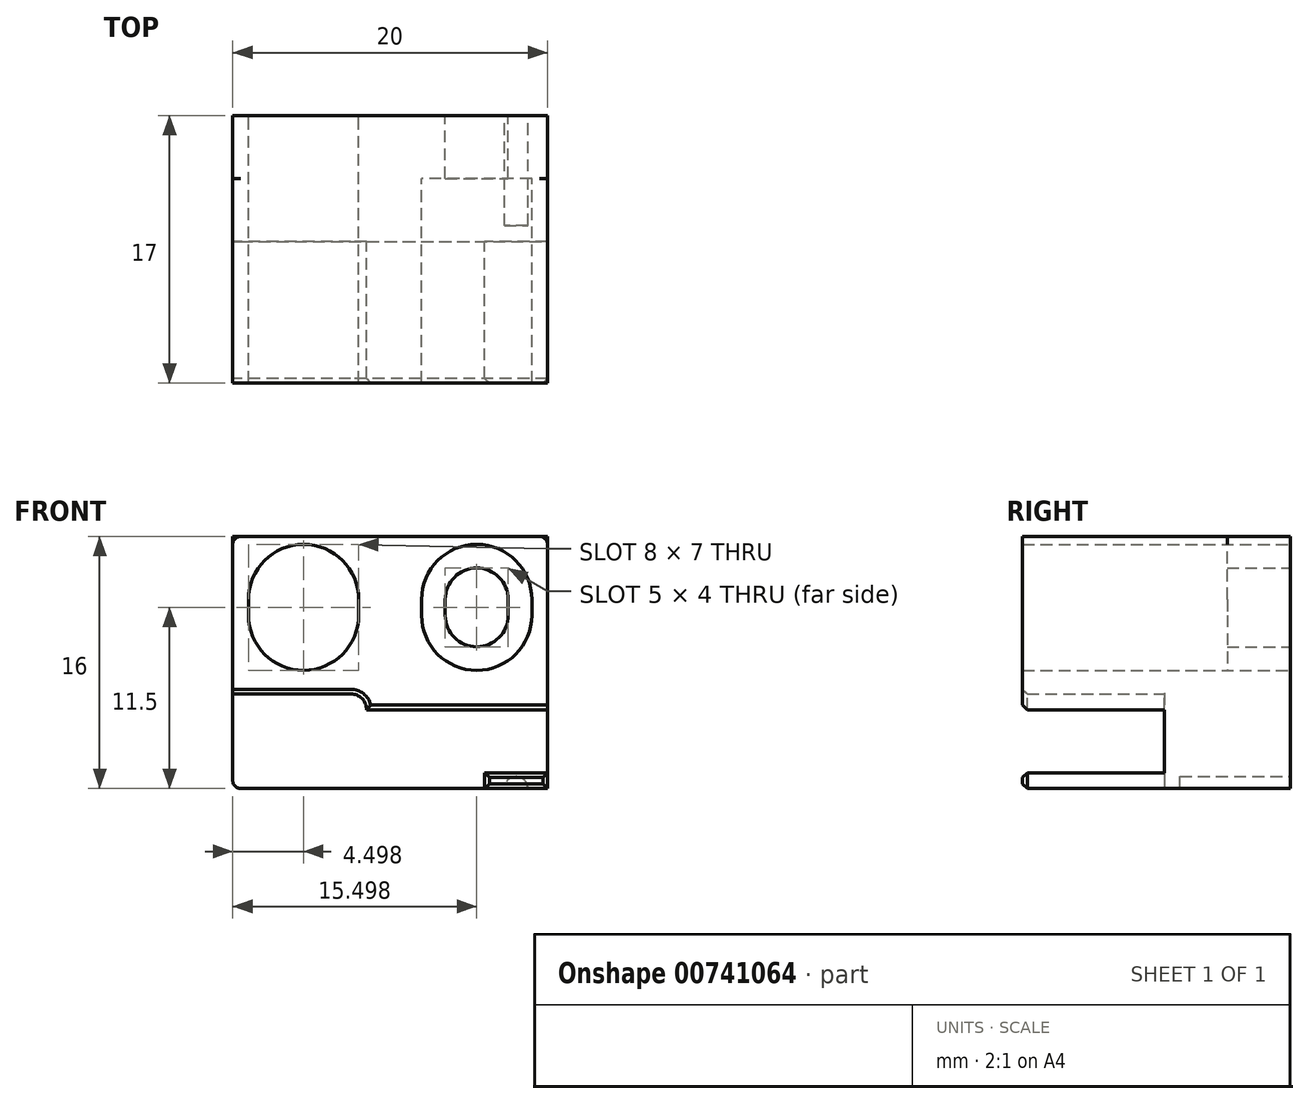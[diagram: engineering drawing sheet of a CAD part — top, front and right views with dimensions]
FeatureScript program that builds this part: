
annotation { "Feature Type Name" : "Feature", "Feature Type Description" : "" }
export const myFeature = defineFeature(function(context is Context, id is Id, definition is map)
    precondition{}
    {
        {
            var Q0;
            Q0=qCreatedBy(makeId("Front.planeOp"),FACE);
            var sketch = newSketch(context, id + "F0", { "sketchPlane" : qUnion([Q0])});
            skLineSegment(sketch, "E0.top", {"start": v(10.79, 11) * mm, "end": v(-9.21, 11) * mm});
            skLineSegment(sketch, "E0.left", {"start": v(10.79, -5) * mm, "end": v(10.79, 11) * mm});
            skLineSegment(sketch, "E0.right", {"start": v(-9.21, 1.06) * mm, "end": v(-9.21, 11) * mm});
            skLineSegment(sketch, "E1", {"start": v(0, 0) * mm, "end": v(10.79, 0) * mm});
            skArc(sketch, "E2.filletArc", {"start": v(-9.21, 1.06) * mm, "mid": v(-9.21, 1.03) * mm, "end": v(-9.2, 1) * mm});
            skLineSegment(sketch, "E3", {"start": v(-9.21, 1.06) * mm, "end": v(-9.21, -4.5) * mm});
            skPoint(sketch, "E4", {"position": v(6.29, 6.5) * mm});
            skArc(sketch, "E5", {"start": v(9.79, 7) * mm, "mid": v(6.29, 10.5) * mm, "end": v(2.79, 7) * mm});
            skArc(sketch, "E6", {"start": v(2.79, 6) * mm, "mid": v(6.29, 2.5) * mm, "end": v(9.79, 6) * mm});
            skLineSegment(sketch, "E7.left", {"start": v(9.79, 7) * mm, "end": v(9.79, 6) * mm});
            skLineSegment(sketch, "E7.right", {"start": v(2.79, 7) * mm, "end": v(2.79, 6) * mm});
            skArc(sketch, "E8", {"start": v(8.29, 7) * mm, "mid": v(6.29, 9) * mm, "end": v(4.29, 7) * mm});
            skArc(sketch, "E9", {"start": v(4.29, 6) * mm, "mid": v(6.29, 4) * mm, "end": v(8.29, 6) * mm});
            skLineSegment(sketch, "E10", {"start": v(4.29, 6) * mm, "end": v(4.29, 7) * mm});
            skLineSegment(sketch, "E11", {"start": v(8.29, 7) * mm, "end": v(8.29, 6) * mm});
            skLineSegment(sketch, "E12", {"start": v(0, 0) * mm, "end": v(-0.71, 0) * mm});
            skLineSegment(sketch, "E13", {"start": v(-0.71, 0) * mm, "end": v(-0.71, 0) * mm});
            skLineSegment(sketch, "E14", {"start": v(-1.71, 1) * mm, "end": v(-9.2, 1) * mm});
            skPoint(sketch, "E15.visualSharp", {"position": v(-0.71, 1) * mm});
            skArc(sketch, "E15.filletArc", {"start": v(-0.71, 0) * mm, "mid": v(-1, 0.7) * mm, "end": v(-1.71, 1) * mm});
            skLineSegment(sketch, "E16", {"start": v(-8.71, -5) * mm, "end": v(10.79, -5) * mm});
            skLineSegment(sketch, "E17", {"start": v(10.79, -4) * mm, "end": v(6.79, -4) * mm});
            skLineSegment(sketch, "E18", {"start": v(6.79, -4) * mm, "end": v(6.79, -5) * mm});
            skPoint(sketch, "E19.visualSharp", {"position": v(-9.21, -5) * mm});
            skArc(sketch, "E19.filletArc", {"start": v(-9.21, -4.5) * mm, "mid": v(-9.07, -4.85) * mm, "end": v(-8.71, -5) * mm});
            skPoint(sketch, "E20", {"position": v(8.79, -5) * mm});
            skArc(sketch, "E21", {"start": v(9.54, -5) * mm, "mid": v(8.79, -4.25) * mm, "end": v(8.04, -5) * mm});
            skPoint(sketch, "E22.MirrorP", {"position": v(-4.71, 6.5) * mm});
            skArc(sketch, "E23.MirrorCS", {"start": v(-8.21, 7) * mm, "mid": v(-4.71, 10.5) * mm, "end": v(-1.21, 7) * mm});
            skArc(sketch, "E24.MirrorCS", {"start": v(-2.71, 6) * mm, "mid": v(-4.71, 4) * mm, "end": v(-6.71, 6) * mm});
            skLineSegment(sketch, "E25.MirrorCS", {"start": v(-2.71, 6) * mm, "end": v(-2.71, 7) * mm});
            skLineSegment(sketch, "E26.MirrorCS", {"start": v(-6.71, 7) * mm, "end": v(-6.71, 6) * mm});
            skArc(sketch, "E27.MirrorCS", {"start": v(-1.21, 6) * mm, "mid": v(-4.71, 2.5) * mm, "end": v(-8.21, 6) * mm});
            skLineSegment(sketch, "E28.MirrorCS", {"start": v(-1.21, 7) * mm, "end": v(-1.21, 6) * mm});
            skLineSegment(sketch, "E29.MirrorCS", {"start": v(-8.21, 7) * mm, "end": v(-8.21, 6) * mm});
            skArc(sketch, "E30.MirrorCS", {"start": v(-6.71, 7) * mm, "mid": v(-4.71, 9) * mm, "end": v(-2.71, 7) * mm});
            skSolve(sketch);
        }
        {
            var Q0;
            {var subQ0=sQuery(id+"F0.wireOp",EDGE,"E0.top");Q0=makeQuery(id+"F0.imprint","IMPRINT",FACE,{"disambiguationData":[TD([[makeQuery(id+"F0.imprint","IMPRINT",EDGE,{"derivedFrom":subQ0}),1.0]])]});}
            extrude(context, id + "F1", {"entities" : qUnion([Q0]), "depth" : 17 * mm, "offsetDistance" : 25 * mm});
        }
        {
            var Q0;
            Q0=makeQuery(id+"F0.imprint","IMPRINT",FACE,{"disambiguationData":[TD([[makeQuery(id+"F0.imprint","IMPRINT",EDGE,{"derivedFrom":sQuery(id+"F0.wireOp",EDGE,"E2.filletArc")}),-1.0]])]});
            extrude(context, id + "F2", {"entities" : qUnion([Q0]), "operationType" : NewBodyOperationType.ADD, "depth" : 8 * mm, "offsetDistance" : 25 * mm});
        }
        {
            var Q0;
            {var subQ3=sQuery(id+"F0.wireOp",EDGE,"E17");Q0=makeQuery(id+"F0.imprint","IMPRINT",FACE,{"disambiguationData":[TD([[makeQuery(id+"F0.imprint","IMPRINT",EDGE,{"derivedFrom":subQ3}),1.0]])]});}
            var Q1;
            {var subQ0=sQuery(id+"F0.wireOp",EDGE,"E21");Q1=makeQuery(id+"F0.imprint","IMPRINT",FACE,{"disambiguationData":[TD([[makeQuery(id+"F0.imprint","IMPRINT",EDGE,{"derivedFrom":subQ0}),1.0]])]});}
            extrude(context, id + "F3", {"entities" : qUnion([Q0, Q1]), "operationType" : NewBodyOperationType.ADD, "depth" : 17 * mm, "offsetDistance" : 25 * mm});
        }
        {
            var Q0;
            Q0=makeQuery(id+"F1.opExtrude","SWEPT_EDGE",EDGE,{"disambiguationData":[OSD([sQuery(id+"F0.wireOp",EDGE,"E0.top"),sQuery(id+"F0.wireOp",EDGE,"E0.right")])]});
            var Q1;
            Q1=makeQuery(id+"F1.opExtrude","SWEPT_EDGE",EDGE,{"disambiguationData":[OSD([sQuery(id+"F0.wireOp",EDGE,"E0.top"),sQuery(id+"F0.wireOp",EDGE,"E0.left")])]});
            fillet(context, id + "F4", {"entities" : qUnion([Q0, Q1]), "radius" : 0.5 * mm, "tangentPropagation" : true, "allowEdgeOverflow" : false});
        }
        {
            var Q0;
            Q0=makeQuery(id+"F0.imprint","IMPRINT",FACE,{"disambiguationData":[TD([[makeQuery(id+"F0.imprint","IMPRINT",EDGE,{"derivedFrom":sQuery(id+"F0.wireOp",EDGE,"E5")}),1.0]])]});
            extrude(context, id + "F5", {"entities" : qUnion([Q0]), "operationType" : NewBodyOperationType.ADD, "depth" : 4 * mm, "offsetDistance" : 25 * mm});
        }
        {
            var Q0;
            Q0=makeQuery(id+"F1.opExtrude","CAP_EDGE",EDGE,{"disambiguationData":[OSD([sQuery(id+"F0.wireOp",EDGE,"E14")])],"isStart":false});
            var Q1;
            Q1=makeQuery(id+"F1.opExtrude","CAP_EDGE",EDGE,{"disambiguationData":[OSD([sQuery(id+"F0.wireOp",EDGE,"E15.filletArc")])],"isStart":false});
            var Q2;
            Q2=makeQuery(id+"F1.opExtrude","CAP_EDGE",EDGE,{"disambiguationData":[OSD([sQuery(id+"F0.wireOp",EDGE,"E1"),sQuery(id+"F0.wireOp",EDGE,"E12")])],"isStart":false});
            var Q3;
            Q3=makeQuery(id+"F3.opExtrude","CAP_EDGE",EDGE,{"disambiguationData":[OSD([sQuery(id+"F0.wireOp",EDGE,"E16")])],"isStart":false});
            var Q4;
            Q4=makeQuery(id+"F3.opExtrude","CAP_EDGE",EDGE,{"disambiguationData":[OSD([sQuery(id+"F0.wireOp",EDGE,"E18")])],"isStart":false});
            var Q5;
            Q5=makeQuery(id+"F3.opExtrude","CAP_EDGE",EDGE,{"disambiguationData":[OSD([sQuery(id+"F0.wireOp",EDGE,"E17")])],"isStart":false});
            var Q6;
            Q6=makeQuery(id+"F3.opExtrude","CAP_EDGE",EDGE,{"disambiguationData":[OSD([sQuery(id+"F0.wireOp",EDGE,"E0.left")])],"isStart":false});
            chamfer(context, id + "F6", {"entities" : qUnion([Q0, Q1, Q2, Q3, Q4, Q5, Q6]), "width" : 0.3 * mm, "tangentPropagation" : true});
        }
        {
            var Q0;
            {var subQ0=sQuery(id+"F0.wireOp",EDGE,"E21");Q0=makeQuery(id+"F0.imprint","IMPRINT",FACE,{"disambiguationData":[TD([[makeQuery(id+"F0.imprint","IMPRINT",EDGE,{"derivedFrom":subQ0}),1.0]])]});}
            var Q1;
            Q1=sQuery(id+"F0.wireOp",EDGE,"E21");
            extrude(context, id + "F7", {"entities" : qUnion([Q0]), "operationType" : NewBodyOperationType.REMOVE, "surfaceEntities" : qUnion([Q1]), "depth" : 7 * mm, "offsetDistance" : 25 * mm});
        }
        {
            var Q0;
            Q0=makeQuery(id+"F0.imprint","IMPRINT",FACE,{"disambiguationData":[TD([[makeQuery(id+"F0.imprint","IMPRINT",EDGE,{"derivedFrom":sQuery(id+"F0.wireOp",EDGE,"E23.MirrorCS")}),-1.0]])]});
            extrude(context, id + "F8", {"entities" : qUnion([Q0]), "operationType" : NewBodyOperationType.ADD, "depth" : 4 * mm, "offsetDistance" : 25 * mm});
        }
    });
